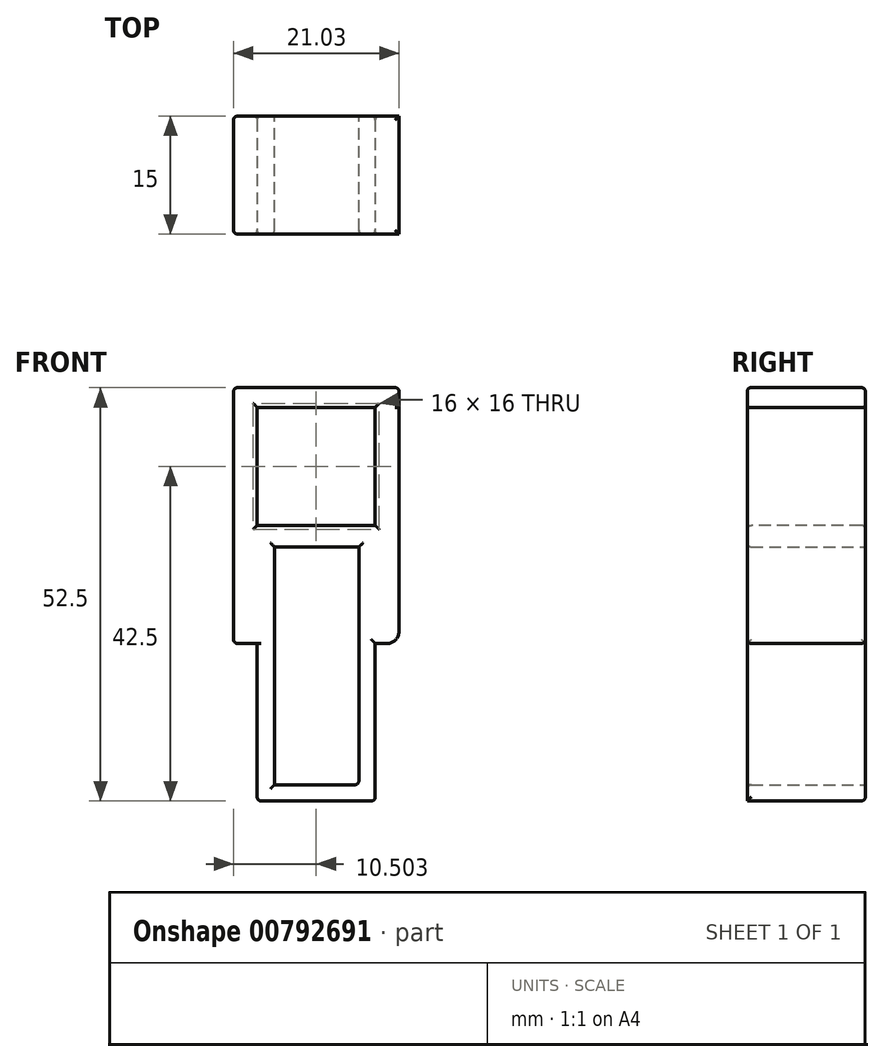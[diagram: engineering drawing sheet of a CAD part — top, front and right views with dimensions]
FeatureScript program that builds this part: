
annotation { "Feature Type Name" : "Feature", "Feature Type Description" : "" }
export const myFeature = defineFeature(function(context is Context, id is Id, definition is map)
    precondition{}
    {
        {
            var Q0;
            Q0=qCreatedBy(makeId("Top.planeOp"),FACE);
            var sketch = newSketch(context, id + "F0", { "sketchPlane" : qUnion([Q0])});
            skLineSegment(sketch, "E0.bottom", {"start": v(-6.63, 6.24) * mm, "end": v(8.37, 6.24) * mm});
            skLineSegment(sketch, "E0.top", {"start": v(-6.63, -8.76) * mm, "end": v(8.37, -8.76) * mm});
            skLineSegment(sketch, "E0.left", {"start": v(-6.63, 6.24) * mm, "end": v(-6.63, -8.76) * mm});
            skLineSegment(sketch, "E0.right", {"start": v(8.37, 6.24) * mm, "end": v(8.37, -8.76) * mm});
            skSolve(sketch);
        }
        {
            var Q0;
            Q0=makeQuery(id+"F0.imprint","IMPRINT",FACE,{"disambiguationData":[TD([[makeQuery(id+"F0.imprint","IMPRINT",EDGE,{"derivedFrom":sQuery(id+"F0.wireOp",EDGE,"E0.bottom")}),-1.0]])]});
            extrude(context, id + "F1", {"entities" : qUnion([Q0]), "depth" : 35 * mm, "offsetDistance" : 25 * mm});
        }
        {
            var Q0;
            Q0=makeQuery(id+"F1.opExtrude","CAP_FACE",FACE,{"disambiguationData":[OSD([sQuery(id+"F0.wireOp",EDGE,"E0.bottom"),sQuery(id+"F0.wireOp",EDGE,"E0.top"),sQuery(id+"F0.wireOp",EDGE,"E0.left"),sQuery(id+"F0.wireOp",EDGE,"E0.right")])],"isStart":false});
            var sketch = newSketch(context, id + "F2", { "sketchPlane" : qUnion([Q0])});
            skLineSegment(sketch, "E1.bottom", {"start": v(-6.63, 6.24) * mm, "end": v(-9.63, 6.24) * mm});
            skLineSegment(sketch, "E1.top", {"start": v(-6.63, -8.76) * mm, "end": v(-9.63, -8.76) * mm});
            skLineSegment(sketch, "E1.left", {"start": v(-6.63, 6.24) * mm, "end": v(-6.63, -8.76) * mm});
            skLineSegment(sketch, "E1.right", {"start": v(-9.63, 6.24) * mm, "end": v(-9.63, -8.76) * mm});
            skLineSegment(sketch, "E2.bottom", {"start": v(8.37, 6.24) * mm, "end": v(11.37, 6.24) * mm});
            skLineSegment(sketch, "E2.top", {"start": v(8.37, -8.76) * mm, "end": v(11.37, -8.76) * mm});
            skLineSegment(sketch, "E2.left", {"start": v(8.37, 6.24) * mm, "end": v(8.37, -8.76) * mm});
            skLineSegment(sketch, "E2.right", {"start": v(11.37, 6.24) * mm, "end": v(11.37, -8.76) * mm});
            skSolve(sketch);
        }
        {
            var Q0;
            Q0 = qSketchRegion(id + "F2", true);
            extrude(context, id + "F3", {"entities" : qUnion([Q0]), "operationType" : NewBodyOperationType.ADD, "endBound" : BoundingType.SYMMETRIC, "depth" : 30 * mm, "offsetDistance" : 25 * mm});
        }
        {
            var Q0;
            Q0=makeQuery(id+"F3.opExtrude","CAP_EDGE",EDGE,{"disambiguationData":[OSD([sQuery(id+"F2.wireOp",EDGE,"E2.right")])],"isStart":true});
            fillet(context, id + "F4", {"entities" : qUnion([Q0]), "radius" : 1.5 * mm, "tangentPropagation" : true, "allowEdgeOverflow" : false});
        }
        {
            var Q0;
            Q0=makeQuery(id+"F3.opExtrude","CAP_FACE",FACE,{"disambiguationData":[OSD([sQuery(id+"F2.wireOp",EDGE,"E1.bottom"),sQuery(id+"F2.wireOp",EDGE,"E1.top"),sQuery(id+"F2.wireOp",EDGE,"E1.left"),sQuery(id+"F2.wireOp",EDGE,"E1.right")])],"isStart":false});
            var sketch = newSketch(context, id + "F5", { "sketchPlane" : qUnion([Q0])});
            skLineSegment(sketch, "E3.bottom", {"start": v(-9.63, 6.24) * mm, "end": v(11.4, 6.24) * mm});
            skLineSegment(sketch, "E3.top", {"start": v(-9.63, -8.76) * mm, "end": v(11.4, -8.76) * mm});
            skLineSegment(sketch, "E3.left", {"start": v(-9.63, 6.24) * mm, "end": v(-9.63, -8.76) * mm});
            skLineSegment(sketch, "E3.right", {"start": v(11.4, 6.24) * mm, "end": v(11.4, -8.76) * mm});
            skSolve(sketch);
        }
        {
            var Q0;
            Q0 = qSketchRegion(id + "F5", true);
            extrude(context, id + "F6", {"entities" : qUnion([Q0]), "operationType" : NewBodyOperationType.ADD, "depth" : 2.5 * mm, "offsetDistance" : 25 * mm});
        }
        {
            var Q0;
            Q0=makeQuery(id+"F6.opExtrude","CAP_EDGE",EDGE,{"disambiguationData":[OSD([sQuery(id+"F5.wireOp",EDGE,"E3.bottom")])],"isStart":false});
            var Q1;
            Q1=makeQuery(id+"F6.opExtrude","CAP_EDGE",EDGE,{"disambiguationData":[OSD([sQuery(id+"F5.wireOp",EDGE,"E3.left")])],"isStart":false});
            var Q2;
            Q2=makeQuery(id+"F6.opExtrude","CAP_EDGE",EDGE,{"disambiguationData":[OSD([sQuery(id+"F5.wireOp",EDGE,"E3.top")])],"isStart":false});
            var Q3;
            Q3=makeQuery(id+"F6.opExtrude","CAP_EDGE",EDGE,{"disambiguationData":[OSD([sQuery(id+"F5.wireOp",EDGE,"E3.right")])],"isStart":false});
            var Q4;
            Q4=makeQuery(id+"F6.boolean.opBoolean","MERGE",EDGE,{"derivedFrom":[makeQuery(id+"F3.opExtrude","SWEPT_EDGE",EDGE,{"disambiguationData":[OSD([sQuery(id+"F2.wireOp",EDGE,"E1.bottom"),sQuery(id+"F2.wireOp",EDGE,"E1.right")])]}),makeQuery(id+"F6.opExtrude","SWEPT_EDGE",EDGE,{"disambiguationData":[OSD([sQuery(id+"F5.wireOp",EDGE,"E3.bottom"),sQuery(id+"F5.wireOp",EDGE,"E3.left")])]})]});
            var Q5;
            Q5=makeQuery(id+"F6.boolean.opBoolean","MERGE",EDGE,{"derivedFrom":[makeQuery(id+"F3.opExtrude","SWEPT_EDGE",EDGE,{"disambiguationData":[OSD([sQuery(id+"F2.wireOp",EDGE,"E1.top"),sQuery(id+"F2.wireOp",EDGE,"E1.right")])]}),makeQuery(id+"F6.opExtrude","SWEPT_EDGE",EDGE,{"disambiguationData":[OSD([sQuery(id+"F5.wireOp",EDGE,"E3.top"),sQuery(id+"F5.wireOp",EDGE,"E3.left")])]})]});
            var Q6;
            Q6=makeQuery(id+"F3.opExtrude","SWEPT_EDGE",EDGE,{"disambiguationData":[OSD([sQuery(id+"F2.wireOp",EDGE,"E2.bottom"),sQuery(id+"F2.wireOp",EDGE,"E2.right")])]});
            var Q7;
            Q7=makeQuery(id+"F1.opExtrude","CAP_EDGE",EDGE,{"disambiguationData":[OSD([sQuery(id+"F0.wireOp",EDGE,"E0.bottom")])],"isStart":false});
            var Q8;
            Q8=makeQuery(id+"F3.opExtrude","SWEPT_EDGE",EDGE,{"disambiguationData":[OSD([sQuery(id+"F0.wireOp",EDGE,"E0.bottom"),sQuery(id+"F2.wireOp",EDGE,"E2.bottom"),sQuery(id+"F2.wireOp",EDGE,"E2.left")])]});
            var Q9;
            {var subQ0=sQuery(id+"F5.wireOp",EDGE,"E3.bottom");Q9=makeQuery(id+"F6.boolean.opBoolean","SPLIT",EDGE,{"disambiguationData":[TD([makeQuery(id+"F3.opExtrude","SWEPT_FACE",FACE,{"disambiguationData":[OSD([sQuery(id+"F2.wireOp",EDGE,"E1.left")])]})])],"derivedFrom":makeQuery(id+"F6.opExtrude","CAP_EDGE",EDGE,{"disambiguationData":[OSD([subQ0])],"isStart":true})});}
            var Q10;
            Q10=makeQuery(id+"F3.opExtrude","SWEPT_EDGE",EDGE,{"disambiguationData":[OSD([sQuery(id+"F0.wireOp",EDGE,"E0.bottom"),sQuery(id+"F2.wireOp",EDGE,"E1.bottom"),sQuery(id+"F2.wireOp",EDGE,"E1.left")])]});
            var Q11;
            Q11=makeQuery(id+"F1.opExtrude","SWEPT_EDGE",EDGE,{"disambiguationData":[OSD([sQuery(id+"F0.wireOp",EDGE,"E0.top"),sQuery(id+"F0.wireOp",EDGE,"E0.left")])]});
            var Q12;
            Q12=makeQuery(id+"F3.opExtrude","CAP_EDGE",EDGE,{"disambiguationData":[OSD([sQuery(id+"F2.wireOp",EDGE,"E1.right")])],"isStart":true});
            var Q13;
            Q13=makeQuery(id+"F1.opExtrude","SWEPT_EDGE",EDGE,{"disambiguationData":[OSD([sQuery(id+"F0.wireOp",EDGE,"E0.bottom"),sQuery(id+"F0.wireOp",EDGE,"E0.left")])]});
            var Q14;
            Q14=makeQuery(id+"F1.opExtrude","CAP_EDGE",EDGE,{"disambiguationData":[OSD([sQuery(id+"F0.wireOp",EDGE,"E0.left")])],"isStart":true});
            var Q15;
            Q15=makeQuery(id+"F1.opExtrude","SWEPT_EDGE",EDGE,{"disambiguationData":[OSD([sQuery(id+"F0.wireOp",EDGE,"E0.bottom"),sQuery(id+"F0.wireOp",EDGE,"E0.right")])]});
            var Q16;
            Q16=makeQuery(id+"F1.opExtrude","CAP_EDGE",EDGE,{"disambiguationData":[OSD([sQuery(id+"F0.wireOp",EDGE,"E0.bottom")])],"isStart":true});
            var Q17;
            Q17=makeQuery(id+"F3.opExtrude","SWEPT_EDGE",EDGE,{"disambiguationData":[OSD([sQuery(id+"F2.wireOp",EDGE,"E2.top"),sQuery(id+"F2.wireOp",EDGE,"E2.right")])]});
            var Q18;
            Q18=makeQuery(id+"F1.opExtrude","SWEPT_EDGE",EDGE,{"disambiguationData":[OSD([sQuery(id+"F0.wireOp",EDGE,"E0.top"),sQuery(id+"F0.wireOp",EDGE,"E0.right")])]});
            var Q19;
            Q19=makeQuery(id+"F1.opExtrude","CAP_EDGE",EDGE,{"disambiguationData":[OSD([sQuery(id+"F0.wireOp",EDGE,"E0.right")])],"isStart":true});
            var Q20;
            {var subQ0=sQuery(id+"F2.wireOp",EDGE,"E2.right");Q20=makeQuery(id+"F4.opFillet","BLEND_EDGE",EDGE,{"blendedFrom":[makeQuery(id+"F3.opExtrude","CAP_EDGE",EDGE,{"disambiguationData":[OSD([subQ0])],"isStart":true}),makeQuery(id+"F3.opExtrude","SWEPT_FACE",FACE,{"disambiguationData":[OSD([subQ0])]})],"blendedInto":[makeQuery(id+"F3.opExtrude","SWEPT_FACE",FACE,{"disambiguationData":[OSD([subQ0])]})]});}
            fillet(context, id + "F7", {"entities" : qUnion([Q0, Q1, Q2, Q3, Q4, Q5, Q6, Q7, Q8, Q9, Q10, Q11, Q12, Q13, Q14, Q15, Q16, Q17, Q18, Q19, Q20]), "radius" : 0.5 * mm, "tangentPropagation" : true, "allowEdgeOverflow" : false});
        }
        {
            var Q0;
            Q0=makeQuery(id+"F6.boolean.opBoolean","MERGE",FACE,{"derivedFrom":[makeQuery(id+"F3.boolean.opBoolean","MERGE",FACE,{"derivedFrom":[makeQuery(id+"F1.opExtrude","SWEPT_FACE",FACE,{"disambiguationData":[OSD([sQuery(id+"F0.wireOp",EDGE,"E0.bottom")])]}),makeQuery(id+"F3.opExtrude","SWEPT_FACE",FACE,{"disambiguationData":[OSD([sQuery(id+"F2.wireOp",EDGE,"E1.bottom")])]}),makeQuery(id+"F3.opExtrude","SWEPT_FACE",FACE,{"disambiguationData":[OSD([sQuery(id+"F2.wireOp",EDGE,"E2.bottom")])]})]}),makeQuery(id+"F6.opExtrude","SWEPT_FACE",FACE,{"disambiguationData":[OSD([sQuery(id+"F5.wireOp",EDGE,"E3.bottom")])]})]});
            var sketch = newSketch(context, id + "F8", { "sketchPlane" : qUnion([Q0])});
            skLineSegment(sketch, "E4.bottom", {"start": v(-6.3, 2.05) * mm, "end": v(4.42, 2.05) * mm});
            skLineSegment(sketch, "E4.top", {"start": v(-6.3, 32.27) * mm, "end": v(4.42, 32.27) * mm});
            skLineSegment(sketch, "E4.left", {"start": v(-6.3, 2.05) * mm, "end": v(-6.3, 32.27) * mm});
            skLineSegment(sketch, "E4.right", {"start": v(4.42, 2.05) * mm, "end": v(4.42, 32.27) * mm});
            skSolve(sketch);
        }
        {
            var Q0;
            Q0 = qSketchRegion(id + "F8", true);
            extrude(context, id + "F9", {"entities" : qUnion([Q0]), "operationType" : NewBodyOperationType.REMOVE, "oppositeDirection" : true, "depth" : 25 * mm, "offsetDistance" : 25 * mm});
        }
        {
            var Q0;
            Q0=makeQuery(id+"F9.boolean.opBoolean","COPY",EDGE,{"derivedFrom":makeQuery(id+"F9.opExtrude","CAP_EDGE",EDGE,{"disambiguationData":[OSD([sQuery(id+"F8.wireOp",EDGE,"E4.left")])],"isStart":true})});
            var Q1;
            Q1=makeQuery(id+"F9.boolean.opBoolean","INTERSECT",EDGE,{"derivedFrom":[makeQuery(id+"F6.boolean.opBoolean","MERGE",FACE,{"derivedFrom":[makeQuery(id+"F3.boolean.opBoolean","MERGE",FACE,{"derivedFrom":[makeQuery(id+"F1.opExtrude","SWEPT_FACE",FACE,{"disambiguationData":[OSD([sQuery(id+"F0.wireOp",EDGE,"E0.top")])]}),makeQuery(id+"F3.opExtrude","SWEPT_FACE",FACE,{"disambiguationData":[OSD([sQuery(id+"F2.wireOp",EDGE,"E1.top")])]}),makeQuery(id+"F3.opExtrude","SWEPT_FACE",FACE,{"disambiguationData":[OSD([sQuery(id+"F2.wireOp",EDGE,"E2.top")])]})]}),makeQuery(id+"F6.opExtrude","SWEPT_FACE",FACE,{"disambiguationData":[OSD([sQuery(id+"F5.wireOp",EDGE,"E3.top")])]})]}),makeQuery(id+"F9.opExtrude","SWEPT_FACE",FACE,{"disambiguationData":[OSD([sQuery(id+"F8.wireOp",EDGE,"E4.left")])]})]});
            var Q2;
            Q2=makeQuery(id+"F9.boolean.opBoolean","COPY",EDGE,{"derivedFrom":makeQuery(id+"F9.opExtrude","CAP_EDGE",EDGE,{"disambiguationData":[OSD([sQuery(id+"F8.wireOp",EDGE,"E4.bottom")])],"isStart":true})});
            var Q3;
            Q3=makeQuery(id+"F9.boolean.opBoolean","COPY",EDGE,{"derivedFrom":makeQuery(id+"F9.opExtrude","SWEPT_EDGE",EDGE,{"disambiguationData":[OSD([sQuery(id+"F8.wireOp",EDGE,"E4.bottom"),sQuery(id+"F8.wireOp",EDGE,"E4.left")])]})});
            var Q4;
            Q4=makeQuery(id+"F9.boolean.opBoolean","INTERSECT",EDGE,{"derivedFrom":[makeQuery(id+"F6.boolean.opBoolean","MERGE",FACE,{"derivedFrom":[makeQuery(id+"F3.boolean.opBoolean","MERGE",FACE,{"derivedFrom":[makeQuery(id+"F1.opExtrude","SWEPT_FACE",FACE,{"disambiguationData":[OSD([sQuery(id+"F0.wireOp",EDGE,"E0.top")])]}),makeQuery(id+"F3.opExtrude","SWEPT_FACE",FACE,{"disambiguationData":[OSD([sQuery(id+"F2.wireOp",EDGE,"E1.top")])]}),makeQuery(id+"F3.opExtrude","SWEPT_FACE",FACE,{"disambiguationData":[OSD([sQuery(id+"F2.wireOp",EDGE,"E2.top")])]})]}),makeQuery(id+"F6.opExtrude","SWEPT_FACE",FACE,{"disambiguationData":[OSD([sQuery(id+"F5.wireOp",EDGE,"E3.top")])]})]}),makeQuery(id+"F9.opExtrude","SWEPT_FACE",FACE,{"disambiguationData":[OSD([sQuery(id+"F8.wireOp",EDGE,"E4.top")])]})]});
            var Q5;
            Q5=makeQuery(id+"F9.boolean.opBoolean","INTERSECT",EDGE,{"derivedFrom":[makeQuery(id+"F6.boolean.opBoolean","MERGE",FACE,{"derivedFrom":[makeQuery(id+"F3.boolean.opBoolean","MERGE",FACE,{"derivedFrom":[makeQuery(id+"F1.opExtrude","SWEPT_FACE",FACE,{"disambiguationData":[OSD([sQuery(id+"F0.wireOp",EDGE,"E0.top")])]}),makeQuery(id+"F3.opExtrude","SWEPT_FACE",FACE,{"disambiguationData":[OSD([sQuery(id+"F2.wireOp",EDGE,"E1.top")])]}),makeQuery(id+"F3.opExtrude","SWEPT_FACE",FACE,{"disambiguationData":[OSD([sQuery(id+"F2.wireOp",EDGE,"E2.top")])]})]}),makeQuery(id+"F6.opExtrude","SWEPT_FACE",FACE,{"disambiguationData":[OSD([sQuery(id+"F5.wireOp",EDGE,"E3.top")])]})]}),makeQuery(id+"F9.opExtrude","SWEPT_FACE",FACE,{"disambiguationData":[OSD([sQuery(id+"F8.wireOp",EDGE,"E4.right")])]})]});
            var Q6;
            Q6=makeQuery(id+"F9.boolean.opBoolean","INTERSECT",EDGE,{"derivedFrom":[makeQuery(id+"F6.boolean.opBoolean","MERGE",FACE,{"derivedFrom":[makeQuery(id+"F3.boolean.opBoolean","MERGE",FACE,{"derivedFrom":[makeQuery(id+"F1.opExtrude","SWEPT_FACE",FACE,{"disambiguationData":[OSD([sQuery(id+"F0.wireOp",EDGE,"E0.top")])]}),makeQuery(id+"F3.opExtrude","SWEPT_FACE",FACE,{"disambiguationData":[OSD([sQuery(id+"F2.wireOp",EDGE,"E1.top")])]}),makeQuery(id+"F3.opExtrude","SWEPT_FACE",FACE,{"disambiguationData":[OSD([sQuery(id+"F2.wireOp",EDGE,"E2.top")])]})]}),makeQuery(id+"F6.opExtrude","SWEPT_FACE",FACE,{"disambiguationData":[OSD([sQuery(id+"F5.wireOp",EDGE,"E3.top")])]})]}),makeQuery(id+"F9.opExtrude","SWEPT_FACE",FACE,{"disambiguationData":[OSD([sQuery(id+"F8.wireOp",EDGE,"E4.bottom")])]})]});
            var Q7;
            {var subQ0=sQuery(id+"F0.wireOp",EDGE,"E0.top");Q7=makeQuery(id+"F7.opFillet","BLEND_EDGE",EDGE,{"blendedFrom":[makeQuery(id+"F1.opExtrude","SWEPT_EDGE",EDGE,{"disambiguationData":[OSD([subQ0,sQuery(id+"F0.wireOp",EDGE,"E0.left")])]}),makeQuery(id+"F6.boolean.opBoolean","MERGE",FACE,{"derivedFrom":[makeQuery(id+"F3.boolean.opBoolean","MERGE",FACE,{"derivedFrom":[makeQuery(id+"F1.opExtrude","SWEPT_FACE",FACE,{"disambiguationData":[OSD([subQ0])]}),makeQuery(id+"F3.opExtrude","SWEPT_FACE",FACE,{"disambiguationData":[OSD([sQuery(id+"F2.wireOp",EDGE,"E1.top")])]}),makeQuery(id+"F3.opExtrude","SWEPT_FACE",FACE,{"disambiguationData":[OSD([sQuery(id+"F2.wireOp",EDGE,"E2.top")])]})]}),makeQuery(id+"F6.opExtrude","SWEPT_FACE",FACE,{"disambiguationData":[OSD([sQuery(id+"F5.wireOp",EDGE,"E3.top")])]})]})],"blendedInto":[makeQuery(id+"F6.boolean.opBoolean","MERGE",FACE,{"derivedFrom":[makeQuery(id+"F3.boolean.opBoolean","MERGE",FACE,{"derivedFrom":[makeQuery(id+"F1.opExtrude","SWEPT_FACE",FACE,{"disambiguationData":[OSD([subQ0])]}),makeQuery(id+"F3.opExtrude","SWEPT_FACE",FACE,{"disambiguationData":[OSD([sQuery(id+"F2.wireOp",EDGE,"E1.top")])]}),makeQuery(id+"F3.opExtrude","SWEPT_FACE",FACE,{"disambiguationData":[OSD([sQuery(id+"F2.wireOp",EDGE,"E2.top")])]})]}),makeQuery(id+"F6.opExtrude","SWEPT_FACE",FACE,{"disambiguationData":[OSD([sQuery(id+"F5.wireOp",EDGE,"E3.top")])]})]})]});}
            var Q8;
            {var subQ0=sQuery(id+"F0.wireOp",EDGE,"E0.left");Q8=makeQuery(id+"F7.opFillet","BLEND_EDGE",EDGE,{"blendedFrom":[makeQuery(id+"F1.opExtrude","CAP_EDGE",EDGE,{"disambiguationData":[OSD([subQ0])],"isStart":true}),makeQuery(id+"F1.opExtrude","CAP_FACE",FACE,{"disambiguationData":[OSD([sQuery(id+"F0.wireOp",EDGE,"E0.bottom"),sQuery(id+"F0.wireOp",EDGE,"E0.top"),subQ0,sQuery(id+"F0.wireOp",EDGE,"E0.right")])],"isStart":true})],"blendedInto":[makeQuery(id+"F1.opExtrude","CAP_FACE",FACE,{"disambiguationData":[OSD([sQuery(id+"F0.wireOp",EDGE,"E0.bottom"),sQuery(id+"F0.wireOp",EDGE,"E0.top"),subQ0,sQuery(id+"F0.wireOp",EDGE,"E0.right")])],"isStart":true})]});}
            var Q9;
            Q9=makeQuery(id+"F9.boolean.opBoolean","COPY",EDGE,{"derivedFrom":makeQuery(id+"F9.opExtrude","CAP_EDGE",EDGE,{"disambiguationData":[OSD([sQuery(id+"F8.wireOp",EDGE,"E4.right")])],"isStart":true})});
            var Q10;
            Q10=makeQuery(id+"F9.boolean.opBoolean","COPY",EDGE,{"derivedFrom":makeQuery(id+"F9.opExtrude","CAP_EDGE",EDGE,{"disambiguationData":[OSD([sQuery(id+"F8.wireOp",EDGE,"E4.top")])],"isStart":true})});
            fillet(context, id + "F10", {"entities" : qUnion([Q0, Q1, Q2, Q3, Q4, Q5, Q6, Q7, Q8, Q9, Q10]), "radius" : 0.5 * mm, "tangentPropagation" : true, "allowEdgeOverflow" : false});
        }
        {
            var Q0;
            {var subQ0=sQuery(id+"F5.wireOp",EDGE,"E3.top");Q0=makeQuery(id+"F6.boolean.opBoolean","SPLIT",EDGE,{"disambiguationData":[TD([makeQuery(id+"F3.opExtrude","SWEPT_FACE",FACE,{"disambiguationData":[OSD([sQuery(id+"F2.wireOp",EDGE,"E1.left")])]})])],"derivedFrom":makeQuery(id+"F6.opExtrude","CAP_EDGE",EDGE,{"disambiguationData":[OSD([subQ0])],"isStart":true})});}
            var Q1;
            Q1=makeQuery(id+"F3.opExtrude","SWEPT_EDGE",EDGE,{"disambiguationData":[OSD([sQuery(id+"F0.wireOp",EDGE,"E0.top"),sQuery(id+"F2.wireOp",EDGE,"E1.top"),sQuery(id+"F2.wireOp",EDGE,"E1.left")])]});
            var Q2;
            Q2=makeQuery(id+"F1.opExtrude","CAP_EDGE",EDGE,{"disambiguationData":[OSD([sQuery(id+"F0.wireOp",EDGE,"E0.top")])],"isStart":false});
            var Q3;
            Q3=makeQuery(id+"F3.opExtrude","SWEPT_EDGE",EDGE,{"disambiguationData":[OSD([sQuery(id+"F0.wireOp",EDGE,"E0.top"),sQuery(id+"F2.wireOp",EDGE,"E2.top"),sQuery(id+"F2.wireOp",EDGE,"E2.left")])]});
            fillet(context, id + "F11", {"entities" : qUnion([Q0, Q1, Q2, Q3]), "radius" : 0.5 * mm, "tangentPropagation" : true, "allowEdgeOverflow" : false});
        }
    });
